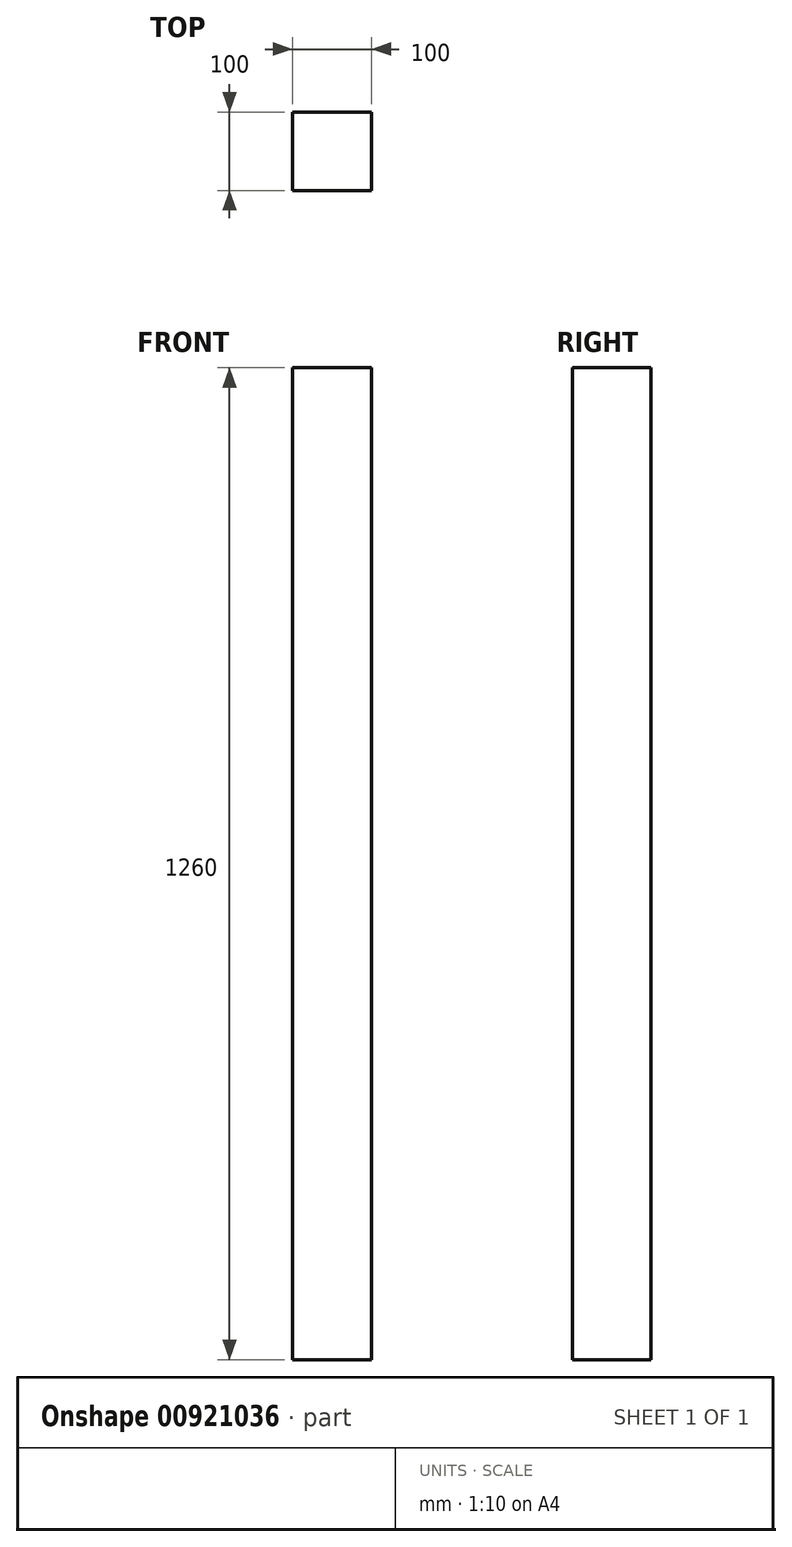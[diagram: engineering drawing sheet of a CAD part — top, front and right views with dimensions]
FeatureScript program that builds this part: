
annotation { "Feature Type Name" : "Feature", "Feature Type Description" : "" }
export const myFeature = defineFeature(function(context is Context, id is Id, definition is map)
    precondition{}
    {
        {
            var Q0;
            Q0=qCreatedBy(makeId("Top.planeOp"),FACE);
            var sketch = newSketch(context, id + "F0", { "sketchPlane" : qUnion([Q0])});
            skLineSegment(sketch, "E0.bottom", {"start": v(50, 50) * mm, "end": v(-50, 50) * mm});
            skLineSegment(sketch, "E0.top", {"start": v(50, -50) * mm, "end": v(-50, -50) * mm});
            skLineSegment(sketch, "E0.left", {"start": v(50, 50) * mm, "end": v(50, -50) * mm});
            skLineSegment(sketch, "E0.right", {"start": v(-50, 50) * mm, "end": v(-50, -50) * mm});
            skPoint(sketch, "E0.middle", {"position": v(0, 0) * mm});
            skSolve(sketch);
        }
        {
            var Q0;
            Q0 = qSketchRegion(id + "F0", true);
            extrude(context, id + "F1", {"entities" : qUnion([Q0]), "depth" : 1260 * mm, "offsetDistance" : 25 * mm});
        }
    });
